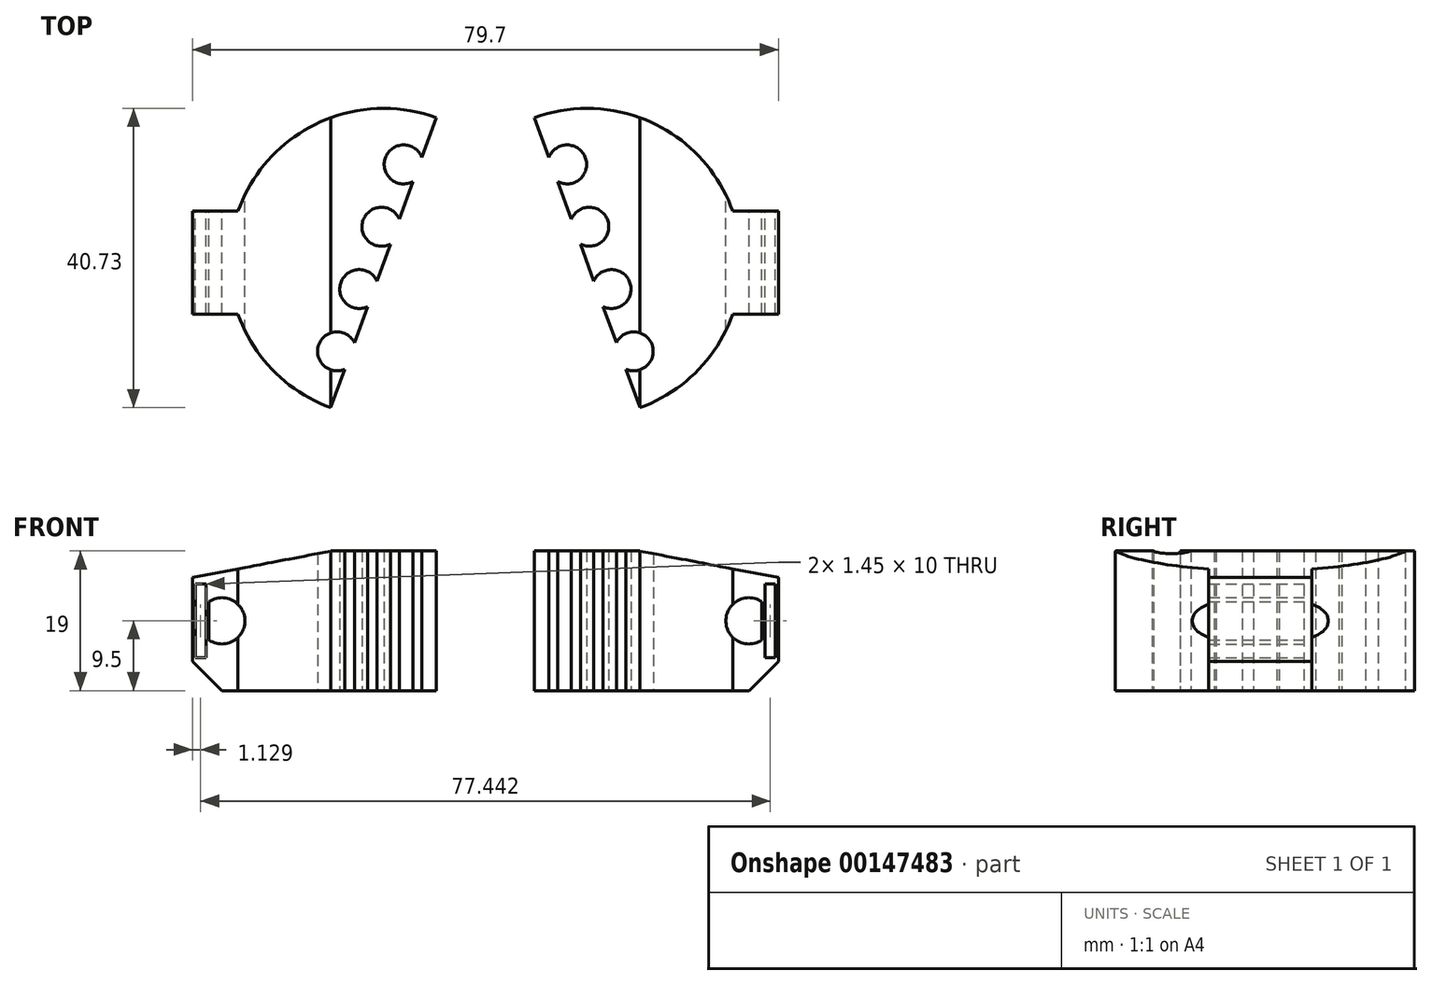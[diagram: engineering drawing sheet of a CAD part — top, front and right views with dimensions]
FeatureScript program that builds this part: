
annotation { "Feature Type Name" : "Feature", "Feature Type Description" : "" }
export const myFeature = defineFeature(function(context is Context, id is Id, definition is map)
    precondition{}
    {
        {
            var Q0;
            Q0=qCreatedBy(makeId("Top.planeOp"),FACE);
            var sketch = newSketch(context, id + "F0", { "sketchPlane" : qUnion([Q0])});
            skArc(sketch, "E0", {"start": v(-13.85, 21) * mm, "mid": v(-34.53, 3.65) * mm, "end": v(-21.03, -19.73) * mm});
            skLineSegment(sketch, "E1.bottom", {"start": v(-26.2, 7) * mm, "end": v(-39.85, 7) * mm});
            skLineSegment(sketch, "E1.top", {"start": v(-26.2, -7) * mm, "end": v(-39.85, -7) * mm});
            skLineSegment(sketch, "E1.left", {"start": v(-26.2, 7) * mm, "end": v(-26.2, -7) * mm});
            skLineSegment(sketch, "E1.right", {"start": v(-39.85, 7) * mm, "end": v(-39.85, -7) * mm});
            skLineSegment(sketch, "E2", {"start": v(-3.72, 27.82) * mm, "end": v(-8.63, 14.32) * mm});
            skArc(sketch, "E3", {"start": v(-8.63, 14.32) * mm, "mid": v(-13.6, 14.28) * mm, "end": v(-9.82, 11.05) * mm});
            skArc(sketch, "E4", {"start": v(-13.85, 21) * mm, "mid": v(-10.2, 20.68) * mm, "end": v(-6.66, 19.73) * mm});
            skArc(sketch, "E5.1.0.0", {"start": v(-11.69, 5.93) * mm, "mid": v(-16.62, 5.8) * mm, "end": v(-12.92, 2.53) * mm});
            skArc(sketch, "E5.2.0.0", {"start": v(-14.75, -2.47) * mm, "mid": v(-19.64, -2.68) * mm, "end": v(-16.02, -5.98) * mm});
            skArc(sketch, "E5.3.0.0", {"start": v(-17.8, -10.88) * mm, "mid": v(-22.66, -11.16) * mm, "end": v(-19.12, -14.5) * mm});
            skLineSegment(sketch, "E5.direction1", {"start": v(-11.1, 13.37) * mm, "end": v(-14.13, 4.9) * mm, "construction": true});
            skLineSegment(sketch, "E6.trimOffspring", {"start": v(-9.82, 11.05) * mm, "end": v(-11.69, 5.93) * mm});
            skLineSegment(sketch, "E7.trimOffspring", {"start": v(-12.92, 2.53) * mm, "end": v(-14.75, -2.47) * mm});
            skLineSegment(sketch, "E8.trimOffspring", {"start": v(-16.02, -5.98) * mm, "end": v(-17.8, -10.88) * mm});
            skLineSegment(sketch, "E9.trimOffspring", {"start": v(-19.12, -14.5) * mm, "end": v(-26.15, -33.82) * mm});
            skSolve(sketch);
        }
        {
            var Q0;
            Q0 = qSketchRegion(id + "F0", true);
            extrude(context, id + "F1", {"entities" : qUnion([Q0]), "depth" : 19 * mm});
        }
        {
            var Q0;
            Q0=makeQuery(id+"F1.opExtrude","SWEPT_FACE",FACE,{"disambiguationData":[OSD([sQuery(id+"F0.wireOp",EDGE,"E1.bottom")])]});
            var sketch = newSketch(context, id + "F2", { "sketchPlane" : qUnion([Q0])});
            skPoint(sketch, "E10.startSnap0", {"position": v(39.85, 9.5) * mm});
            skArc(sketch, "E11", {"start": v(37.6, 12.12) * mm, "mid": v(32.7, 9.5) * mm, "end": v(37.6, 6.88) * mm});
            skLineSegment(sketch, "E12.bottom", {"start": v(39.45, 4.5) * mm, "end": v(38, 4.5) * mm});
            skLineSegment(sketch, "E12.top", {"start": v(39.45, 14.5) * mm, "end": v(38, 14.5) * mm});
            skLineSegment(sketch, "E12.left", {"start": v(39.45, 4.5) * mm, "end": v(39.45, 14.5) * mm});
            skLineSegment(sketch, "E12.right", {"start": v(38, 4.5) * mm, "end": v(38, 7.2) * mm});
            skLineSegment(sketch, "E13.trimOffspring", {"start": v(38, 11.8) * mm, "end": v(38, 14.5) * mm});
            skPoint(sketch, "E14.MirrorP", {"position": v(41.73, 3.62) * mm});
            skLineSegment(sketch, "E15", {"start": v(43.66, 9.5) * mm, "end": v(5.71, 9.5) * mm, "construction": true});
            skLineSegment(sketch, "E16", {"start": v(40.8, 15.2) * mm, "end": v(18.13, 19.55) * mm});
            skLineSegment(sketch, "E17", {"start": v(18.13, 19.55) * mm, "end": v(40.8, 19.55) * mm});
            skLineSegment(sketch, "E18", {"start": v(40.8, 19.55) * mm, "end": v(40.8, 15.2) * mm});
            skLineSegment(sketch, "E19", {"start": v(38, 13.83) * mm, "end": v(38, 5.85) * mm});
            skLineSegment(sketch, "E20", {"start": v(37.6, 5.85) * mm, "end": v(37.6, 12.12) * mm});
            skSolve(sketch);
        }
        {
            var Q0;
            Q0 = qSketchRegion(id + "F2", true);
            extrude(context, id + "F3", {"entities" : qUnion([Q0]), "operationType" : NewBodyOperationType.REMOVE, "endBound" : BoundingType.THROUGH_ALL, "oppositeDirection" : true, "depth" : 25 * mm, "hasSecondDirection" : true, "secondDirectionBound" : SecondDirectionBoundingType.THROUGH_ALL, "secondDirectionOppositeDirection" : false, "secondDirectionDepth" : 25 * mm});
        }
        {
            var Q0;
            Q0=makeQuery(id+"F1.opExtrude","CAP_EDGE",EDGE,{"disambiguationData":[OSD([sQuery(id+"F0.wireOp",EDGE,"E1.right")])],"isStart":true});
            chamfer(context, id + "F4", {"entities" : qUnion([Q0]), "width" : 4 * mm, "tangentPropagation" : true});
        }
        {
            var Q0;
            Q0=makeQuery(id+"F1.opExtrude","SWEPT_BODY",BODY,{"disambiguationData":[OSD([sQuery(id+"F0.wireOp",EDGE,"E0"),sQuery(id+"F0.wireOp",EDGE,"95N6hNCV-rWDU-Wu4v-AaLr-48t5X6IrUOdN"),sQuery(id+"F0.wireOp",EDGE,"E1.bottom"),sQuery(id+"F0.wireOp",EDGE,"E1.top"),sQuery(id+"F0.wireOp",EDGE,"E1.right"),sQuery(id+"F0.wireOp",EDGE,"9fqSe68T-KitM-dttq-r3eB-JhlcNs2OKoLA"),sQuery(id+"F0.wireOp",EDGE,"9e5a13be-1e01-4b59-a197-64b462a7910e.1.0.0"),sQuery(id+"F0.wireOp",EDGE,"9e5a13be-1e01-4b59-a197-64b462a7910e.2.0.0"),sQuery(id+"F0.wireOp",EDGE,"9e5a13be-1e01-4b59-a197-64b462a7910e.3.0.0"),sQuery(id+"F0.wireOp",EDGE,"4d30c7f7-ad06-4893-9c86-bbe4aa07bb10.trimOffspring"),sQuery(id+"F0.wireOp",EDGE,"0c8c3122-39b8-4ebe-bd3d-40b6193792e5.trimOffspring"),sQuery(id+"F0.wireOp",EDGE,"7856b111-24d2-4a84-bdb2-69175ae554ea.trimOffspring"),sQuery(id+"F0.wireOp",EDGE,"c9447546-2868-441d-b27c-64921e5a4e09.trimOffspring")])]});
            var Q1;
            Q1=qCreatedBy(makeId("Right.planeOp"),FACE);
            mirror(context, id + "F5", {"entities" : qUnion([Q0]), "mirrorPlane" : qUnion([Q1])});
        }
    });
